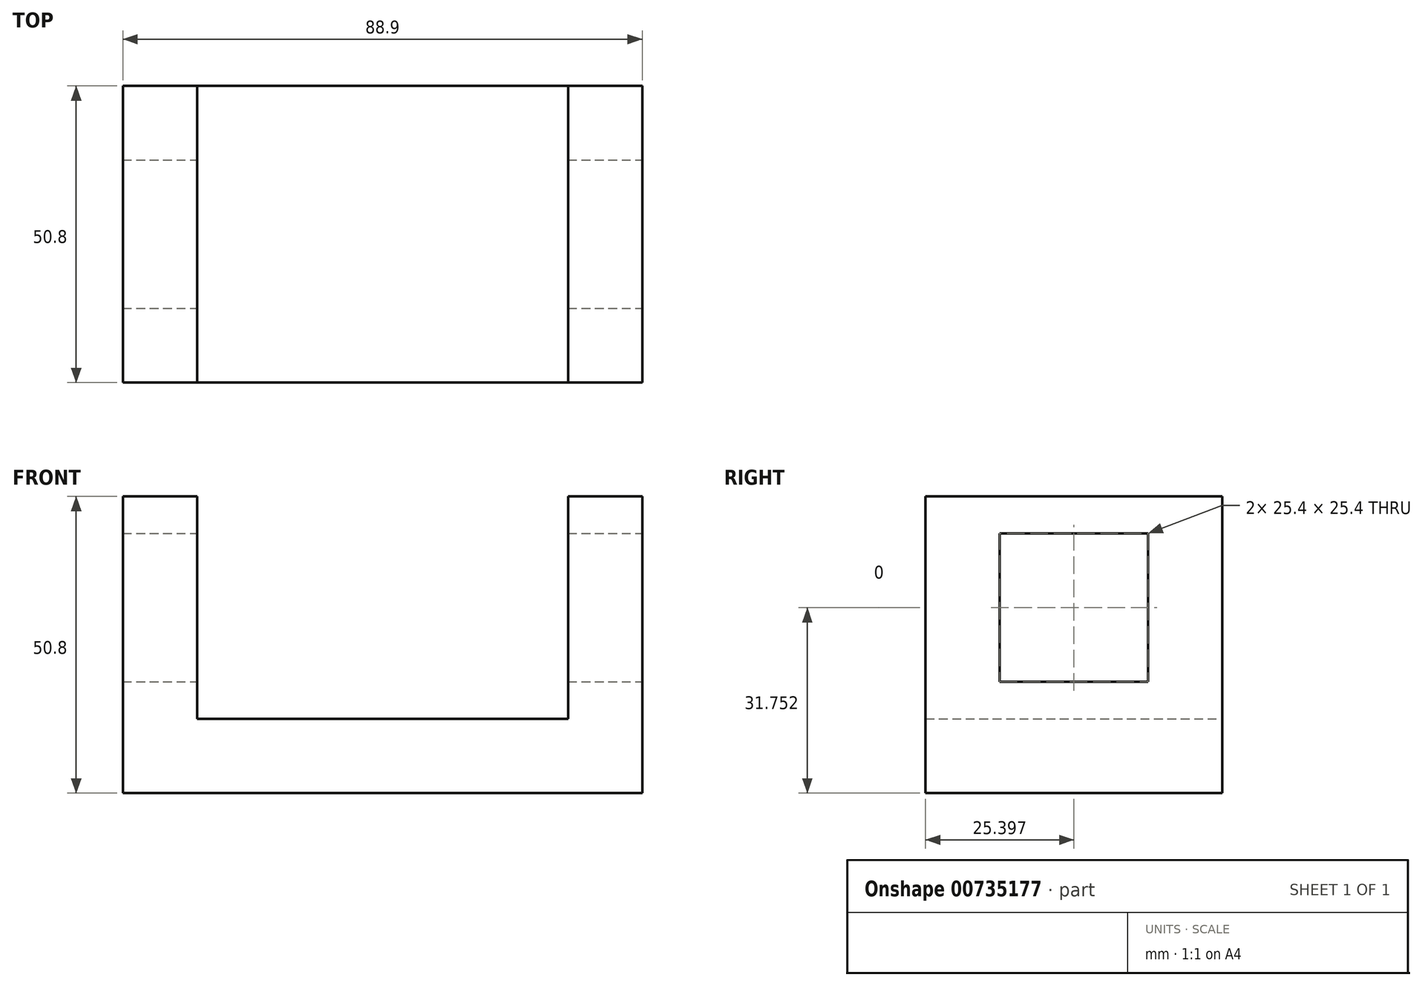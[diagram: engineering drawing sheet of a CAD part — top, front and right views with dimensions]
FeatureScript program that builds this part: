
annotation { "Feature Type Name" : "Feature", "Feature Type Description" : "" }
export const myFeature = defineFeature(function(context is Context, id is Id, definition is map)
    precondition{}
    {
        {
            var Q0;
            Q0=qCreatedBy(makeId("Right.planeOp"),FACE);
            var sketch = newSketch(context, id + "F0", { "sketchPlane" : qUnion([Q0])});
            skLineSegment(sketch, "E0.bottom", {"start": v(-37.84, 37.63) * mm, "end": v(12.96, 37.63) * mm});
            skLineSegment(sketch, "E0.top", {"start": v(-37.84, -13.17) * mm, "end": v(12.96, -13.17) * mm});
            skLineSegment(sketch, "E0.left", {"start": v(-37.84, 37.63) * mm, "end": v(-37.84, -13.17) * mm});
            skLineSegment(sketch, "E0.right", {"start": v(12.96, 37.63) * mm, "end": v(12.96, -13.17) * mm});
            skLineSegment(sketch, "E1.bottom", {"start": v(-25.14, 31.28) * mm, "end": v(0.26, 31.28) * mm});
            skLineSegment(sketch, "E1.top", {"start": v(-25.14, 5.88) * mm, "end": v(0.26, 5.88) * mm});
            skLineSegment(sketch, "E1.left", {"start": v(-25.14, 31.28) * mm, "end": v(-25.14, 5.88) * mm});
            skLineSegment(sketch, "E1.right", {"start": v(0.26, 31.28) * mm, "end": v(0.26, 5.88) * mm});
            skSolve(sketch);
        }
        {
            var Q0;
            Q0=makeQuery(id+"F0.imprint","IMPRINT",FACE,{"disambiguationData":[TD([[makeQuery(id+"F0.imprint","IMPRINT",EDGE,{"derivedFrom":sQuery(id+"F0.wireOp",EDGE,"E0.bottom")}),-1.0]])]});
            extrude(context, id + "F1", {"entities" : qUnion([Q0]), "oppositeDirection" : true, "depth" : 88.9 * mm, "offsetDistance" : 25.4 * mm});
        }
        {
            var Q0;
            Q0=makeQuery(id+"F1.opExtrude","SWEPT_FACE",FACE,{"disambiguationData":[OSD([sQuery(id+"F0.wireOp",EDGE,"E0.right")])]});
            var sketch = newSketch(context, id + "F2", { "sketchPlane" : qUnion([Q0])});
            skLineSegment(sketch, "E2", {"start": v(12.7, 37.63) * mm, "end": v(12.7, -0.47) * mm});
            skLineSegment(sketch, "E3", {"start": v(76.2, -0.47) * mm, "end": v(12.7, -0.47) * mm});
            skLineSegment(sketch, "E4", {"start": v(76.2, -0.47) * mm, "end": v(76.2, 37.63) * mm});
            skSolve(sketch);
        }
        {
            var Q0;
            Q0 = qSketchRegion(id + "F2", true);
            var Q1;
            {var subQ0=sQuery(id+"F2.wireOp",EDGE,"E2");Q1=makeQuery(id+"F2.imprint","IMPRINT",FACE,{"disambiguationData":[TD([[makeQuery(id+"F2.imprint","IMPRINT",EDGE,{"derivedFrom":subQ0}),1.0]])]});}
            extrude(context, id + "F3", {"entities" : qUnion([Q0, Q1]), "operationType" : NewBodyOperationType.REMOVE, "oppositeDirection" : true, "depth" : 152.4 * mm, "offsetDistance" : 25.4 * mm});
        }
    });
